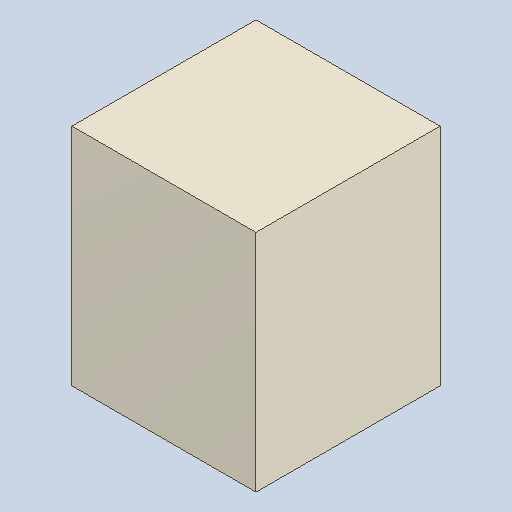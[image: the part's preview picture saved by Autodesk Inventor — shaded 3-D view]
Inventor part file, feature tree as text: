
AUTODESK INVENTOR PART (.ipt)
format: ipt  version: 2023.4 (Build 274418000, 418)  size: 82,944 bytes
history: native  units: mm
features: extrude x1
ambient origin geometry x8: Origin, YZ Plane, XZ Plane, XY Plane, X Axis, Y Axis, Z Axis, Center Point
bodies: Solid1 (feature_tree)
feature tree (1):
  extrude  "Extruded_6"  [1 undecoded]
note: 1 required parameter value undecoded (feature->parameter linkage not recoverable at this tier; creation-order binding heuristic only, values carry confidence <= 0.55)
